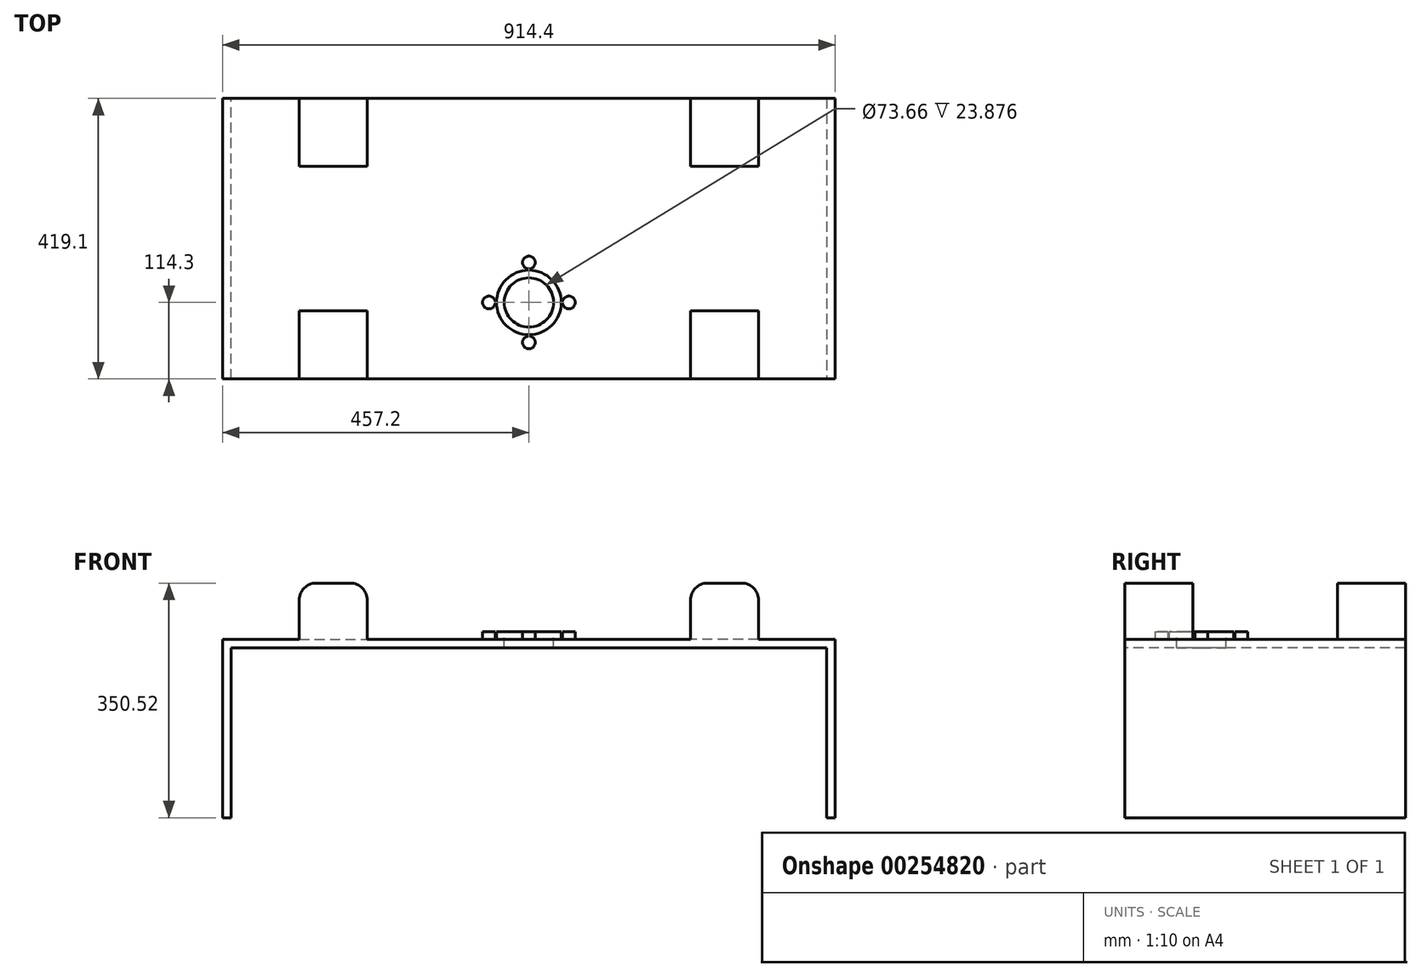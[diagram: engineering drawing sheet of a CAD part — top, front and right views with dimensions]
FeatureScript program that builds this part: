
annotation { "Feature Type Name" : "Feature", "Feature Type Description" : "" }
export const myFeature = defineFeature(function(context is Context, id is Id, definition is map)
    precondition{}
    {
        {
            var Q0;
            Q0=qCreatedBy(makeId("Top.planeOp"),FACE);
            var sketch = newSketch(context, id + "F0", { "sketchPlane" : qUnion([Q0])});
            skLineSegment(sketch, "E0.bottom", {"start": v(-457.2, 304.8) * mm, "end": v(457.2, 304.8) * mm});
            skLineSegment(sketch, "E0.top", {"start": v(-457.2, -114.3) * mm, "end": v(457.2, -114.3) * mm});
            skLineSegment(sketch, "E0.left", {"start": v(-457.2, 304.8) * mm, "end": v(-457.2, -114.3) * mm});
            skLineSegment(sketch, "E0.right", {"start": v(457.2, 304.8) * mm, "end": v(457.2, -114.3) * mm});
            skSolve(sketch);
        }
        {
            var Q0;
            Q0=makeQuery(id+"F0.imprint","IMPRINT",FACE,{"disambiguationData":[TD([[makeQuery(id+"F0.imprint","IMPRINT",EDGE,{"derivedFrom":sQuery(id+"F0.wireOp",EDGE,"E0.bottom")}),-1.0]])]});
            extrude(context, id + "F1", {"entities" : qUnion([Q0]), "depth" : 12.7 * mm});
        }
        {
            var Q0;
            Q0=makeQuery(id+"F1.opExtrude","CAP_FACE",FACE,{"disambiguationData":[OSD([sQuery(id+"F0.wireOp",EDGE,"E0.bottom"),sQuery(id+"F0.wireOp",EDGE,"E0.top"),sQuery(id+"F0.wireOp",EDGE,"E0.left"),sQuery(id+"F0.wireOp",EDGE,"E0.right")])],"isStart":false});
            var sketch = newSketch(context, id + "F2", { "sketchPlane" : qUnion([Q0])});
            skCircle(sketch, "E1", {"center": v(0, 0) * mm, "radius": 36.83 * mm});
            skSolve(sketch);
        }
        {
            var Q0;
            Q0=makeQuery(id+"F2.imprint","IMPRINT",FACE,{"disambiguationData":[TD([[makeQuery(id+"F2.imprint","IMPRINT",EDGE,{"derivedFrom":sQuery(id+"F2.wireOp",EDGE,"E1")}),1.0]])]});
            extrude(context, id + "F3", {"entities" : qUnion([Q0]), "operationType" : NewBodyOperationType.REMOVE, "oppositeDirection" : true, "depth" : 12.7 * mm});
        }
        {
            var Q0;
            Q0=makeQuery(id+"F1.opExtrude","CAP_FACE",FACE,{"disambiguationData":[OSD([sQuery(id+"F0.wireOp",EDGE,"E0.bottom"),sQuery(id+"F0.wireOp",EDGE,"E0.top"),sQuery(id+"F0.wireOp",EDGE,"E0.left"),sQuery(id+"F0.wireOp",EDGE,"E0.right")])],"isStart":false});
            var sketch = newSketch(context, id + "F4", { "sketchPlane" : qUnion([Q0])});
            skCircle(sketch, "E2", {"center": v(0, 0) * mm, "radius": 48.26 * mm});
            skCircle(sketch, "E3", {"center": v(0, 0) * mm, "radius": 36.83 * mm});
            skLineSegment(sketch, "E4", {"start": v(0, 0) * mm, "end": v(0, 59.7) * mm});
            skLineSegment(sketch, "E5", {"start": v(0, 0) * mm, "end": v(0, -59.7) * mm});
            skLineSegment(sketch, "E6", {"start": v(0, 0) * mm, "end": v(-59.7, 0) * mm});
            skLineSegment(sketch, "E7", {"start": v(0, 0) * mm, "end": v(59.7, 0) * mm});
            skCircle(sketch, "E8", {"center": v(0, 59.7) * mm, "radius": 9.53 * mm});
            skCircle(sketch, "E9", {"center": v(-59.7, 0) * mm, "radius": 9.53 * mm});
            skCircle(sketch, "E10", {"center": v(0, -59.7) * mm, "radius": 9.53 * mm});
            skCircle(sketch, "E11", {"center": v(59.7, 0) * mm, "radius": 9.53 * mm});
            skSolve(sketch);
        }
        {
            var Q0;
            Q0=makeQuery(id+"F4.imprint","IMPRINT",FACE,{"disambiguationData":[TD([[makeQuery(id+"F4.imprint","IMPRINT",EDGE,{"derivedFrom":sQuery(id+"F4.wireOp",EDGE,"E8")}),1.0]])]});
            var Q1;
            Q1=makeQuery(id+"F4.imprint","IMPRINT",FACE,{"disambiguationData":[TD([[makeQuery(id+"F4.imprint","IMPRINT",EDGE,{"derivedFrom":sQuery(id+"F4.wireOp",EDGE,"E2")}),1.0]])]});
            var Q2;
            Q2=makeQuery(id+"F4.imprint","IMPRINT",FACE,{"disambiguationData":[TD([[makeQuery(id+"F4.imprint","IMPRINT",EDGE,{"derivedFrom":sQuery(id+"F4.wireOp",EDGE,"E9")}),1.0]])]});
            var Q3;
            Q3=makeQuery(id+"F4.imprint","IMPRINT",FACE,{"disambiguationData":[TD([[makeQuery(id+"F4.imprint","IMPRINT",EDGE,{"derivedFrom":sQuery(id+"F4.wireOp",EDGE,"E10")}),1.0]])]});
            var Q4;
            Q4=makeQuery(id+"F4.imprint","IMPRINT",FACE,{"disambiguationData":[TD([[makeQuery(id+"F4.imprint","IMPRINT",EDGE,{"derivedFrom":sQuery(id+"F4.wireOp",EDGE,"E11")}),1.0]])]});
            extrude(context, id + "F5", {"entities" : qUnion([Q0, Q1, Q2, Q3, Q4]), "operationType" : NewBodyOperationType.ADD, "depth" : 11.18 * mm});
        }
        {
            var Q0;
            Q0=makeQuery(id+"F1.opExtrude","CAP_FACE",FACE,{"disambiguationData":[OSD([sQuery(id+"F0.wireOp",EDGE,"E0.bottom"),sQuery(id+"F0.wireOp",EDGE,"E0.top"),sQuery(id+"F0.wireOp",EDGE,"E0.left"),sQuery(id+"F0.wireOp",EDGE,"E0.right")])],"isStart":false});
            var sketch = newSketch(context, id + "F6", { "sketchPlane" : qUnion([Q0])});
            skLineSegment(sketch, "E12.bottom", {"start": v(-342.9, 304.8) * mm, "end": v(-241.3, 304.8) * mm});
            skLineSegment(sketch, "E12.top", {"start": v(-342.9, 203.2) * mm, "end": v(-241.3, 203.2) * mm});
            skLineSegment(sketch, "E12.left", {"start": v(-342.9, 304.8) * mm, "end": v(-342.9, 203.2) * mm});
            skLineSegment(sketch, "E12.right", {"start": v(-241.3, 304.8) * mm, "end": v(-241.3, 203.2) * mm});
            skLineSegment(sketch, "E13.bottom", {"start": v(-342.9, -114.3) * mm, "end": v(-241.3, -114.3) * mm});
            skLineSegment(sketch, "E13.top", {"start": v(-342.9, -12.7) * mm, "end": v(-241.3, -12.7) * mm});
            skLineSegment(sketch, "E13.left", {"start": v(-342.9, -114.3) * mm, "end": v(-342.9, -12.7) * mm});
            skLineSegment(sketch, "E13.right", {"start": v(-241.3, -114.3) * mm, "end": v(-241.3, -12.7) * mm});
            skLineSegment(sketch, "E14.bottom", {"start": v(241.3, 304.8) * mm, "end": v(342.9, 304.8) * mm});
            skLineSegment(sketch, "E14.top", {"start": v(241.3, 203.2) * mm, "end": v(342.9, 203.2) * mm});
            skLineSegment(sketch, "E14.left", {"start": v(241.3, 304.8) * mm, "end": v(241.3, 203.2) * mm});
            skLineSegment(sketch, "E14.right", {"start": v(342.9, 304.8) * mm, "end": v(342.9, 203.2) * mm});
            skLineSegment(sketch, "E15.bottom", {"start": v(342.9, -114.3) * mm, "end": v(241.3, -114.3) * mm});
            skLineSegment(sketch, "E15.top", {"start": v(342.9, -12.7) * mm, "end": v(241.3, -12.7) * mm});
            skLineSegment(sketch, "E15.left", {"start": v(342.9, -114.3) * mm, "end": v(342.9, -12.7) * mm});
            skLineSegment(sketch, "E15.right", {"start": v(241.3, -114.3) * mm, "end": v(241.3, -12.7) * mm});
            skSolve(sketch);
        }
        {
            var Q0;
            Q0=makeQuery(id+"F6.imprint","IMPRINT",FACE,{"disambiguationData":[TD([[makeQuery(id+"F6.imprint","IMPRINT",EDGE,{"derivedFrom":sQuery(id+"F6.wireOp",EDGE,"E12.bottom")}),-1.0]])]});
            var Q1;
            Q1=makeQuery(id+"F6.imprint","IMPRINT",FACE,{"disambiguationData":[TD([[makeQuery(id+"F6.imprint","IMPRINT",EDGE,{"derivedFrom":sQuery(id+"F6.wireOp",EDGE,"E13.bottom")}),1.0]])]});
            var Q2;
            Q2=makeQuery(id+"F6.imprint","IMPRINT",FACE,{"disambiguationData":[TD([[makeQuery(id+"F6.imprint","IMPRINT",EDGE,{"derivedFrom":sQuery(id+"F6.wireOp",EDGE,"E15.bottom")}),1.0]])]});
            var Q3;
            Q3=makeQuery(id+"F6.imprint","IMPRINT",FACE,{"disambiguationData":[TD([[makeQuery(id+"F6.imprint","IMPRINT",EDGE,{"derivedFrom":sQuery(id+"F6.wireOp",EDGE,"E14.bottom")}),-1.0]])]});
            extrude(context, id + "F7", {"entities" : qUnion([Q0, Q1, Q2, Q3]), "operationType" : NewBodyOperationType.ADD, "depth" : 83.82 * mm});
        }
        {
            var Q0;
            Q0=makeQuery(id+"F1.opExtrude","CAP_FACE",FACE,{"disambiguationData":[OSD([sQuery(id+"F0.wireOp",EDGE,"E0.bottom"),sQuery(id+"F0.wireOp",EDGE,"E0.top"),sQuery(id+"F0.wireOp",EDGE,"E0.left"),sQuery(id+"F0.wireOp",EDGE,"E0.right")])],"isStart":true});
            var sketch = newSketch(context, id + "F8", { "sketchPlane" : qUnion([Q0])});
            skLineSegment(sketch, "E16.bottom", {"start": v(-457.2, 114.3) * mm, "end": v(-444.5, 114.3) * mm});
            skLineSegment(sketch, "E16.top", {"start": v(-457.2, -304.8) * mm, "end": v(-444.5, -304.8) * mm});
            skLineSegment(sketch, "E16.left", {"start": v(-457.2, 114.3) * mm, "end": v(-457.2, -304.8) * mm});
            skLineSegment(sketch, "E16.right", {"start": v(-444.5, 114.3) * mm, "end": v(-444.5, -304.8) * mm});
            skLineSegment(sketch, "E17.bottom", {"start": v(457.2, -304.8) * mm, "end": v(444.5, -304.8) * mm});
            skLineSegment(sketch, "E17.top", {"start": v(457.2, 114.3) * mm, "end": v(444.5, 114.3) * mm});
            skLineSegment(sketch, "E17.left", {"start": v(457.2, -304.8) * mm, "end": v(457.2, 114.3) * mm});
            skLineSegment(sketch, "E17.right", {"start": v(444.5, -304.8) * mm, "end": v(444.5, 114.3) * mm});
            skSolve(sketch);
        }
        {
            var Q0;
            Q0=makeQuery(id+"F8.imprint","IMPRINT",FACE,{"disambiguationData":[TD([[makeQuery(id+"F8.imprint","IMPRINT",EDGE,{"derivedFrom":sQuery(id+"F8.wireOp",EDGE,"E16.bottom")}),-1.0]])]});
            var Q1;
            Q1=makeQuery(id+"F8.imprint","IMPRINT",FACE,{"disambiguationData":[TD([[makeQuery(id+"F8.imprint","IMPRINT",EDGE,{"derivedFrom":sQuery(id+"F8.wireOp",EDGE,"E17.bottom")}),1.0]])]});
            extrude(context, id + "F9", {"entities" : qUnion([Q0, Q1]), "operationType" : NewBodyOperationType.ADD, "depth" : 254 * mm});
        }
        {
            var Q0;
            Q0=makeQuery(id+"F7.opExtrude","CAP_EDGE",EDGE,{"disambiguationData":[OSD([sQuery(id+"F6.wireOp",EDGE,"E13.left")])],"isStart":false});
            var Q1;
            Q1=makeQuery(id+"F7.opExtrude","CAP_EDGE",EDGE,{"disambiguationData":[OSD([sQuery(id+"F6.wireOp",EDGE,"E12.left")])],"isStart":false});
            var Q2;
            Q2=makeQuery(id+"F7.opExtrude","CAP_EDGE",EDGE,{"disambiguationData":[OSD([sQuery(id+"F6.wireOp",EDGE,"E12.right")])],"isStart":false});
            var Q3;
            Q3=makeQuery(id+"F7.opExtrude","CAP_EDGE",EDGE,{"disambiguationData":[OSD([sQuery(id+"F6.wireOp",EDGE,"E13.right")])],"isStart":false});
            var Q4;
            Q4=makeQuery(id+"F7.opExtrude","CAP_EDGE",EDGE,{"disambiguationData":[OSD([sQuery(id+"F6.wireOp",EDGE,"E15.right")])],"isStart":false});
            var Q5;
            Q5=makeQuery(id+"F7.opExtrude","CAP_EDGE",EDGE,{"disambiguationData":[OSD([sQuery(id+"F6.wireOp",EDGE,"E14.left")])],"isStart":false});
            var Q6;
            Q6=makeQuery(id+"F7.opExtrude","CAP_EDGE",EDGE,{"disambiguationData":[OSD([sQuery(id+"F6.wireOp",EDGE,"E14.right")])],"isStart":false});
            var Q7;
            Q7=makeQuery(id+"F7.opExtrude","CAP_EDGE",EDGE,{"disambiguationData":[OSD([sQuery(id+"F6.wireOp",EDGE,"E15.left")])],"isStart":false});
            fillet(context, id + "F10", {"entities" : qUnion([Q0, Q1, Q2, Q3, Q4, Q5, Q6, Q7]), "radius" : 25.4 * mm, "tangentPropagation" : true, "allowEdgeOverflow" : false});
        }
    });
